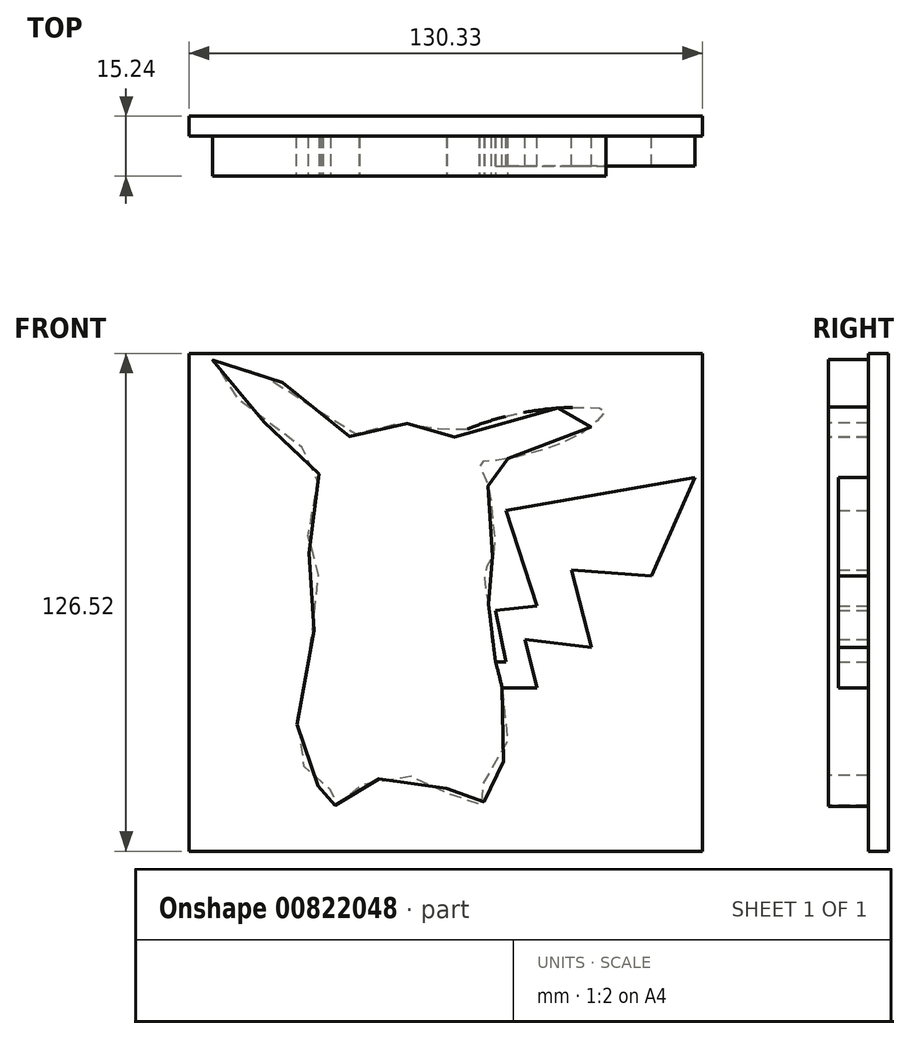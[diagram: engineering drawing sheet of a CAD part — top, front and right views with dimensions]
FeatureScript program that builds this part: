
annotation { "Feature Type Name" : "Feature", "Feature Type Description" : "" }
export const myFeature = defineFeature(function(context is Context, id is Id, definition is map)
    precondition{}
    {
        {
            var Q0;
            Q0=qCreatedBy(makeId("Front.planeOp"),FACE);
            var sketch = newSketch(context, id + "F0", { "sketchPlane" : qUnion([Q0])});
            skFitSpline(sketch, "E0", {"points": [v(-16.52, 39.79) * mm, v(-14.62, 40.23) * mm, v(-9.35, 42.25) * mm, v(-1.96, 43.15) * mm, v(2.3, 42.59) * mm, v(7.67, 41.47) * mm, v(10.8, 39.56) * mm, v(11.48, 40) * mm, v(29.06, 45.95) * mm, v(49.45, 46.62) * mm, v(49.23, 45.95) * mm, v(45.64, 42.14) * mm, v(34.78, 36.76) * mm, v(21.9, 33.74) * mm, v(17.86, 33.29) * mm, v(17.42, 32.73) * mm, v(19.54, 27.58) * mm, v(21, 16.49) * mm, v(21.22, 10.55) * mm, v(18.87, 5.85) * mm, v(18.76, 2.94) * mm, v(19.32, -0.87) * mm, v(20.33, -6.7) * mm, v(20.44, -12.4) * mm, v(21.5, -17.46) * mm, v(23.8, -27.2) * mm, v(24.58, -36.27) * mm, v(22.68, -44.33) * mm, v(17.42, -49.37) * mm, v(17.42, -50.04) * mm, v(18.65, -52.28) * mm, v(17.86, -53.85) * mm, v(14.17, -53.74) * mm, v(9.13, -50.94) * mm, v(9.13, -49.7) * mm, v(1.73, -46.9) * mm, v(-5.88, -46.68) * mm, v(-13.05, -49.37) * mm, v(-13.05, -50.72) * mm, v(-17.3, -53.63) * mm, v(-22.01, -53.52) * mm, v(-22.23, -52.5) * mm, v(-20.44, -49.93) * mm, v(-22.57, -49.6) * mm, v(-26.5, -45.12) * mm, v(-28.96, -38.73) * mm, v(-28.28, -28.76) * mm, v(-25.6, -14.99) * mm, v(-23.58, 5.18) * mm, v(-25.03, 7.08) * mm, v(-26.04, 15.48) * mm, v(-24.59, 24.1) * mm, v(-22.8, 33.85) * mm, v(-23.02, 34.19) * mm, v(-37.47, 43.6) * mm, v(-47.1, 53.45) * mm, v(-50.32, 59.2) * mm, v(-49.45, 59.2) * mm, v(-39.04, 55.91) * mm, v(-27.05, 49.87) * mm, v(-16.52, 39.79) * mm]});
            skLineSegment(sketch, "E1", {"start": v(21.5, -17.46) * mm, "end": v(24.15, -17.46) * mm});
            skLineSegment(sketch, "E2", {"start": v(24.15, -17.46) * mm, "end": v(21.5, -4.46) * mm});
            skLineSegment(sketch, "E3", {"start": v(21.5, -4.46) * mm, "end": v(32.06, -3.24) * mm});
            skLineSegment(sketch, "E4", {"start": v(32.06, -3.24) * mm, "end": v(24.15, 20.97) * mm});
            skLineSegment(sketch, "E5", {"start": v(24.15, 20.97) * mm, "end": v(72.18, 29.35) * mm});
            skLineSegment(sketch, "E6", {"start": v(72.18, 29.35) * mm, "end": v(61.16, 4.3) * mm});
            skLineSegment(sketch, "E7", {"start": v(61.16, 4.3) * mm, "end": v(40.82, 5.9) * mm});
            skLineSegment(sketch, "E8", {"start": v(40.82, 5.9) * mm, "end": v(45.9, -13.79) * mm});
            skLineSegment(sketch, "E9", {"start": v(45.9, -13.79) * mm, "end": v(28.95, -11.81) * mm});
            skLineSegment(sketch, "E10", {"start": v(28.95, -11.81) * mm, "end": v(32.06, -24.15) * mm});
            skLineSegment(sketch, "E11", {"start": v(32.06, -24.15) * mm, "end": v(23.2, -24.15) * mm});
            skSolve(sketch);
        }
        {
            var Q0;
            Q0=makeQuery(id+"F0.imprint","IMPRINT",FACE,{"disambiguationData":[TD([[makeQuery(id+"F0.imprint","IMPRINT",EDGE,{"derivedFrom":sQuery(id+"F0.wireOp",EDGE,"E0")}),-1.0]])]});
            extrude(context, id + "F1", {"entities" : qUnion([Q0]), "depth" : 10.16 * mm});
        }
        {
            var Q0;
            {var subQ0=sQuery(id+"F0.wireOp",EDGE,"E1");Q0=makeQuery(id+"F0.imprint","IMPRINT",FACE,{"disambiguationData":[TD([[makeQuery(id+"F0.imprint","IMPRINT",EDGE,{"derivedFrom":subQ0}),-1.0]])]});}
            extrude(context, id + "F2", {"entities" : qUnion([Q0]), "operationType" : NewBodyOperationType.ADD, "depth" : 7.62 * mm});
        }
        {
            var Q0;
            {var subQ0=sQuery(id+"F0.wireOp",EDGE,"E0");Q0=makeQuery(id+"F2.boolean.opBoolean","MERGE",FACE,{"derivedFrom":[makeQuery(id+"F1.opExtrude","CAP_FACE",FACE,{"disambiguationData":[OSD([subQ0])],"isStart":true}),makeQuery(id+"F2.opExtrude","CAP_FACE",FACE,{"disambiguationData":[OSD([subQ0,sQuery(id+"F0.wireOp",EDGE,"E1"),sQuery(id+"F0.wireOp",EDGE,"E2"),sQuery(id+"F0.wireOp",EDGE,"E3"),sQuery(id+"F0.wireOp",EDGE,"E4"),sQuery(id+"F0.wireOp",EDGE,"E5"),sQuery(id+"F0.wireOp",EDGE,"E6"),sQuery(id+"F0.wireOp",EDGE,"E7"),sQuery(id+"F0.wireOp",EDGE,"E8"),sQuery(id+"F0.wireOp",EDGE,"E9"),sQuery(id+"F0.wireOp",EDGE,"E10"),sQuery(id+"F0.wireOp",EDGE,"E11")])],"isStart":true})]});}
            var sketch = newSketch(context, id + "F3", { "sketchPlane" : qUnion([Q0])});
            skLineSegment(sketch, "E12.bottom", {"start": v(56.3, 60.9) * mm, "end": v(-74.03, 60.9) * mm});
            skLineSegment(sketch, "E12.top", {"start": v(56.3, -65.62) * mm, "end": v(-74.03, -65.62) * mm});
            skLineSegment(sketch, "E12.left", {"start": v(56.3, 60.9) * mm, "end": v(56.3, -65.62) * mm});
            skLineSegment(sketch, "E12.right", {"start": v(-74.03, 60.9) * mm, "end": v(-74.03, -65.62) * mm});
            skSolve(sketch);
        }
        {
            var Q0;
            Q0 = qSketchRegion(id + "F3", true);
            extrude(context, id + "F4", {"entities" : qUnion([Q0]), "operationType" : NewBodyOperationType.ADD, "depth" : 5.08 * mm, "offsetDistance" : 25.4 * mm});
        }
    });
